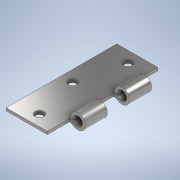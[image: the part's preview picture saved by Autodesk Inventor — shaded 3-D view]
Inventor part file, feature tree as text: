
AUTODESK INVENTOR PART (.ipt)
format: ipt  version: 2021 (Build 250183000, 183)  size: 164,864 bytes
history: native  units: mm
features: extrude x3, sketch x3
ambient origin geometry x8: Origin, YZ Plane, XZ Plane, XY Plane, X Axis, Y Axis, Z Axis, Center Point
bodies: Solid1 (feature_tree)
feature tree (6):
  extrude  "Extrusion1"  Depth=2.5mm
  extrude  "Extrusion2"  Depth=100.0mm TaperAngle=0.0deg
  extrude  "Extrusion3"  Depth=100.0mm
  sketch  "Sketch1"  dims[d1=2.5mm d2=2.5mm]
  sketch  "Sketch2"  dims[d3=8.5mm d4=100.0mm d5=0.0mm]
  sketch  "Sketch3"  dims[d6=8.0mm d7=8.0mm d8=8.0mm d9=10.0mm d10=20.0mm d11=20.0mm d12=10.0mm d13=10.0mm d14=50.0mm d15=100.0mm d16=-3.490659mm d17=20.0mm d18=30.0mm d19=20.0mm d20=20.0mm d21=20.0mm d22=100.0mm d23=0.0mm]
